# Revit family: KEUCO_54985010800
name_source: partatom
category: Allgemeines Modell
revit_build: Autodesk Revit 2016 (Build: 20150220_1215(x64)
units: mm (PartAtom-declared; Revit-internal decimal feet)

## family parameters
Arbeitsebenenbasiert = Ja
Beim Laden mit Abzugskörper schneiden = Nein
Bemaßung runder Anschluss = Durchmesser verwenden
Gemeinsam genutzt = Nein
Immer vertikal = Nein
Kann Basisbauteil für Bewehrung sein = Nein
Raumberechnungspunkt = Nein
Teiletyp = Normal

## types (3) — shared parameters
Hersteller = KEUCO
Material Stange = 850 mm  [stored 2.78871 ft]
Serie = Plan
Typenbild = <Keine Auswahl>
URL = https://www.keuco.com
Verwendung = DU / WA
Vorgabe-Ansicht = 1219 mm
zero-valued in all types: Gewicht

## per-type parameters (varying)
| type | Ausschreibungstext | Beschreibung | Stange Material |
| 54985010800 | KEUCO PLAN Brausestange 54985010800
hochglanzverchromte Brausestange 
in ästhetischem, funktionalem Design
für die Wandmontage, bestehend aus:
- Wandstange mit Brauseschieber, Länge 800 mm, 
  Gesamtlänge 850 mm Höhenverstellung mit Griff, 
  Neigungswinkel stufenlos verstellbar
- Fliesenausgleichsscheibe (5 mm)
Ausladung 67 mm
Die Brausestange wird verdeckt angebracht,
Lieferung inkl. korrosionsfreiem Befestigungsmaterial | bestehend aus:
- Wandstange 800 mm mit Brauseschieber,
  Höhenverstellung mit Griff, Neigungswinkel verstellbar
- mit Fliesenausgleichscheibe (5 mm) | Edelstahl |
| 54985070800 | KEUCO PLAN Brausestange 54985070800
Brausestange in Edelstahl,
in ästhetischem, funktionalem Design
für die Wandmontage, bestehend aus:
- Wandstange mit Brauseschieber, Länge 800 mm, 
  Gesamtlänge 850 mm Höhenverstellung mit Griff, 
  Neigungswinkel stufenlos verstellbar
- Fliesenausgleichsscheibe (5 mm)
Ausladung 67 mm
Die Brausestange wird verdeckt angebracht,
Lieferung inkl. korrosionsfreiem Befestigungsmaterial | bestehend aus:
- Wandstange 800 mm mit Brauseschieber,
 Höhenverstellung mit Griff, Neigungswinkel
 stufenlos verstellbar
- mit Fliesenausgleichscheibe (5 mm) | Edelstahl |
| 54985170800 | KEUCO PLAN Brausestange 54985170800
Brausestange in Aluminium-finish,
in ästhetischem, funktionalem Design
für die Wandmontage, bestehend aus:
- Wandstange mit Brauseschieber, Länge 800 mm, 
  Gesamtlänge 850 mm Höhenverstellung mit Griff, 
  Neigungswinkel stufenlos verstellbar
- Fliesenausgleichsscheibe (5 mm)
Ausladung 67 mm
Die Brausestange wird verdeckt angebracht,
Lieferung inkl. korrosionsfreiem Befestigungsmaterial | bestehend aus:
- Wandstange 800 mm mit Brauseschieber,
 Höhenverstellung mit Griff, Neigungswinkel
 stufenlos verstellbar
- mit Fliesenausgleichscheibe (5 mm) | Aluminium 1100-H18 |

note: column(s) folded — value = type name in every type: Artikelnummer

note: [stored X ft] marks values corroborated as IEEE doubles in the binary element streams (Revit-internal decimal feet)

## geometry (parser evidence)
native form markers: Blend x4, Sweep x2
no freeform markers — native parametric forms only
